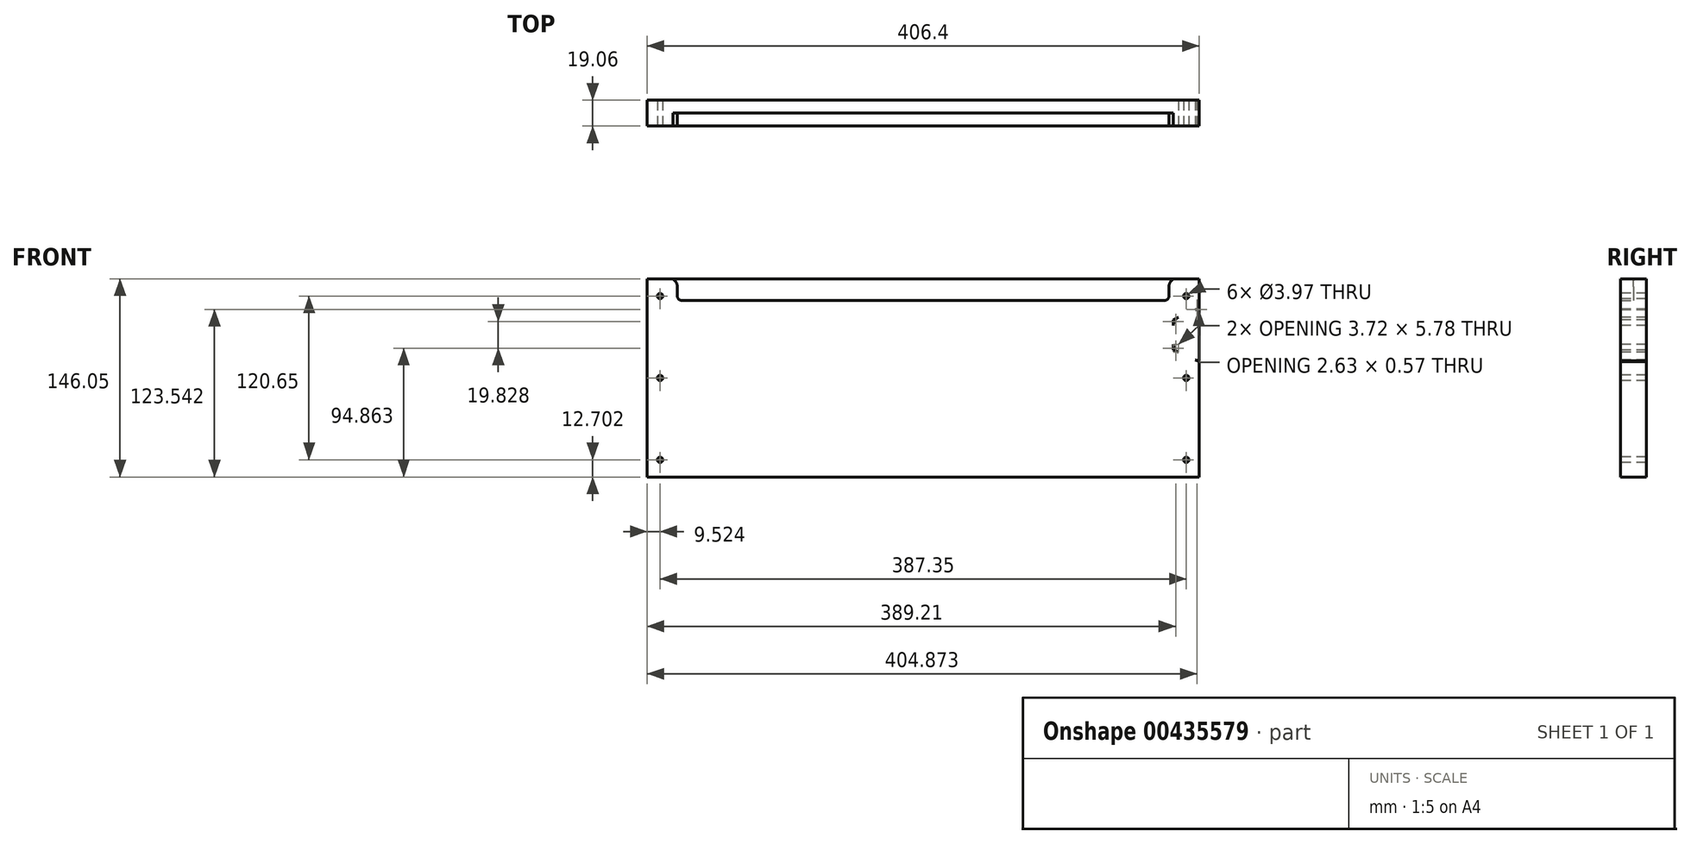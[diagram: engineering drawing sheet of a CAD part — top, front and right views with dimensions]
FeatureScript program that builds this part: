
annotation { "Feature Type Name" : "Feature", "Feature Type Description" : "" }
export const myFeature = defineFeature(function(context is Context, id is Id, definition is map)
    precondition{}
    {
        {
            var Q0;
            Q0=qCreatedBy(makeId("Front.planeOp"),FACE);
            var sketch = newSketch(context, id + "F0", { "sketchPlane" : qUnion([Q0])});
            skLineSegment(sketch, "E0", {"start": v(160.66, 42.77) * mm, "end": v(160.66, 55.47) * mm});
            skLineSegment(sketch, "E1.right", {"start": v(182.89, 55.47) * mm, "end": v(182.89, -90.58) * mm});
            skLineSegment(sketch, "E2", {"start": v(182.89, -30.25) * mm, "end": v(182.68, -30.25) * mm});
            skLineSegment(sketch, "E3", {"start": v(180.05, -30.82) * mm, "end": v(167.56, -36.5) * mm});
            skLineSegment(sketch, "E4", {"start": v(163.84, -42.28) * mm, "end": v(163.84, -56.33) * mm});
            skLineSegment(sketch, "E5", {"start": v(167.56, -62.1) * mm, "end": v(180.05, -67.78) * mm});
            skLineSegment(sketch, "E6", {"start": v(182.68, -68.35) * mm, "end": v(182.89, -68.35) * mm});
            skPoint(sketch, "E7.visualSharp", {"position": v(181.3, -30.25) * mm});
            skArc(sketch, "E7.filletArc", {"start": v(182.68, -30.25) * mm, "mid": v(181.33, -30.4) * mm, "end": v(180.05, -30.82) * mm});
            skPoint(sketch, "E8.visualSharp", {"position": v(163.84, -38.2) * mm});
            skArc(sketch, "E8.filletArc", {"start": v(167.56, -36.5) * mm, "mid": v(164.85, -38.84) * mm, "end": v(163.84, -42.28) * mm});
            skPoint(sketch, "E9.visualSharp", {"position": v(163.84, -60.42) * mm});
            skArc(sketch, "E9.filletArc", {"start": v(163.84, -56.33) * mm, "mid": v(164.85, -59.76) * mm, "end": v(167.56, -62.1) * mm});
            skPoint(sketch, "E10.visualSharp", {"position": v(181.3, -68.35) * mm});
            skArc(sketch, "E10.filletArc", {"start": v(180.05, -67.78) * mm, "mid": v(181.33, -68.2) * mm, "end": v(182.68, -68.35) * mm});
            skLineSegment(sketch, "E11.MirrorCS", {"start": v(-223.51, 55.47) * mm, "end": v(-223.51, -90.58) * mm});
            skArc(sketch, "E12.filletArc", {"start": v(-201.29, 42.77) * mm, "mid": v(-200.36, 40.53) * mm, "end": v(-198.11, 39.6) * mm});
            skArc(sketch, "E13.filletArc", {"start": v(157.49, 39.6) * mm, "mid": v(159.73, 40.53) * mm, "end": v(160.66, 42.77) * mm});
            skLineSegment(sketch, "E14.MirrorCS", {"start": v(182.68, 33.25) * mm, "end": v(182.89, 33.25) * mm});
            skLineSegment(sketch, "E15.MirrorCS", {"start": v(182.89, -4.85) * mm, "end": v(182.68, -4.85) * mm});
            skArc(sketch, "E16.MirrorCS", {"start": v(180.05, 32.68) * mm, "mid": v(181.33, 33.1) * mm, "end": v(182.68, 33.25) * mm});
            skArc(sketch, "E17.MirrorCS", {"start": v(182.68, -4.85) * mm, "mid": v(181.33, -4.7) * mm, "end": v(180.05, -4.28) * mm});
            skArc(sketch, "E18.MirrorCS", {"start": v(163.84, 21.22) * mm, "mid": v(164.85, 24.66) * mm, "end": v(167.56, 27) * mm});
            skLineSegment(sketch, "E19.MirrorCS", {"start": v(157.45, 22.4) * mm, "end": v(189.24, 36.85) * mm});
            skLineSegment(sketch, "E20.MirrorCS", {"start": v(189.24, -8.46) * mm, "end": v(157.45, 5.99) * mm});
            skLineSegment(sketch, "E21.MirrorCS", {"start": v(189.24, -4.85) * mm, "end": v(173.36, -4.85) * mm});
            skLineSegment(sketch, "E22.MirrorCS", {"start": v(173.36, 33.25) * mm, "end": v(189.24, 33.25) * mm});
            skArc(sketch, "E23.MirrorCS", {"start": v(167.56, 1.4) * mm, "mid": v(164.85, 3.74) * mm, "end": v(163.84, 7.17) * mm});
            skLineSegment(sketch, "E24.MirrorCS", {"start": v(180.05, -4.28) * mm, "end": v(167.56, 1.4) * mm});
            skLineSegment(sketch, "E25.MirrorCS", {"start": v(163.84, 7.17) * mm, "end": v(163.84, 21.22) * mm});
            skLineSegment(sketch, "E26.MirrorCS", {"start": v(167.56, 27) * mm, "end": v(180.05, 32.68) * mm});
            skLineSegment(sketch, "E27.MirrorCS", {"start": v(163.84, -1.68) * mm, "end": v(163.84, 36.42) * mm});
            skPoint(sketch, "E28.MirrorP", {"position": v(181.3, -4.85) * mm});
            skPoint(sketch, "E29.MirrorP", {"position": v(163.84, 25.3) * mm});
            skPoint(sketch, "E30.MirrorP", {"position": v(163.84, 3.08) * mm});
            skPoint(sketch, "E31.MirrorP", {"position": v(181.3, 33.25) * mm});
            skLineSegment(sketch, "E32.MirrorCS", {"start": v(-223.3, 33.25) * mm, "end": v(-223.51, 33.25) * mm});
            skLineSegment(sketch, "E33.MirrorCS", {"start": v(-223.51, -4.85) * mm, "end": v(-223.3, -4.85) * mm});
            skLineSegment(sketch, "E34.MirrorCS", {"start": v(-223.3, -68.35) * mm, "end": v(-223.51, -68.35) * mm});
            skArc(sketch, "E35.MirrorCS", {"start": v(-223.3, -30.25) * mm, "mid": v(-221.95, -30.4) * mm, "end": v(-220.67, -30.82) * mm});
            skArc(sketch, "E36.MirrorCS", {"start": v(-220.67, 32.68) * mm, "mid": v(-221.95, 33.1) * mm, "end": v(-223.3, 33.25) * mm});
            skArc(sketch, "E37.MirrorCS", {"start": v(-223.3, -4.85) * mm, "mid": v(-221.95, -4.7) * mm, "end": v(-220.67, -4.28) * mm});
            skArc(sketch, "E38.MirrorCS", {"start": v(-220.67, -67.78) * mm, "mid": v(-221.95, -68.2) * mm, "end": v(-223.3, -68.35) * mm});
            skLineSegment(sketch, "E39.MirrorCS", {"start": v(-223.51, -30.25) * mm, "end": v(-223.3, -30.25) * mm});
            skArc(sketch, "E40.MirrorCS", {"start": v(-208.18, -36.5) * mm, "mid": v(-205.47, -38.84) * mm, "end": v(-204.46, -42.28) * mm});
            skLineSegment(sketch, "E41.MirrorCS", {"start": v(-220.67, -4.28) * mm, "end": v(-208.18, 1.4) * mm});
            skArc(sketch, "E42.MirrorCS", {"start": v(-208.18, 1.4) * mm, "mid": v(-205.47, 3.74) * mm, "end": v(-204.46, 7.17) * mm});
            skArc(sketch, "E43.MirrorCS", {"start": v(-204.46, -56.33) * mm, "mid": v(-205.47, -59.76) * mm, "end": v(-208.18, -62.1) * mm});
            skArc(sketch, "E44.MirrorCS", {"start": v(-204.46, 21.22) * mm, "mid": v(-205.47, 24.66) * mm, "end": v(-208.18, 27) * mm});
            skLineSegment(sketch, "E45.MirrorCS", {"start": v(-220.67, -30.82) * mm, "end": v(-208.18, -36.5) * mm});
            skLineSegment(sketch, "E46.MirrorCS", {"start": v(-208.18, 27) * mm, "end": v(-220.67, 32.68) * mm});
            skLineSegment(sketch, "E47.MirrorCS", {"start": v(-208.18, -62.1) * mm, "end": v(-220.67, -67.78) * mm});
            skPoint(sketch, "E48.MirrorP", {"position": v(-204.46, 3.08) * mm});
            skPoint(sketch, "E49.MirrorP", {"position": v(-204.46, -38.2) * mm});
            skPoint(sketch, "E50.MirrorP", {"position": v(-221.92, 33.25) * mm});
            skPoint(sketch, "E51.MirrorP", {"position": v(-204.46, 25.3) * mm});
            skLineSegment(sketch, "E52.MirrorCS", {"start": v(-204.46, 7.17) * mm, "end": v(-204.46, 21.22) * mm});
            skPoint(sketch, "E53.MirrorP", {"position": v(-221.92, -68.35) * mm});
            skPoint(sketch, "E54.MirrorP", {"position": v(-204.46, -60.42) * mm});
            skLineSegment(sketch, "E55.MirrorCS", {"start": v(-204.46, -42.28) * mm, "end": v(-204.46, -56.33) * mm});
            skPoint(sketch, "E56.MirrorP", {"position": v(-221.92, -30.25) * mm});
            skPoint(sketch, "E57.MirrorP", {"position": v(-221.92, -4.85) * mm});
            skCircle(sketch, "E58", {"center": v(173.36, -77.88) * mm, "radius": 1.98 * mm});
            skCircle(sketch, "E59", {"center": v(173.36, -17.55) * mm, "radius": 1.98 * mm});
            skCircle(sketch, "E60.MirrorC", {"center": v(173.36, 42.77) * mm, "radius": 1.98 * mm});
            skCircle(sketch, "E61.MirrorC", {"center": v(-213.99, -77.88) * mm, "radius": 1.98 * mm});
            skCircle(sketch, "E62.MirrorC", {"center": v(-213.99, -17.55) * mm, "radius": 1.98 * mm});
            skCircle(sketch, "E63.MirrorC", {"center": v(-213.99, 42.77) * mm, "radius": 1.98 * mm});
            skLineSegment(sketch, "E64", {"start": v(-201.29, 55.47) * mm, "end": v(-201.29, 42.77) * mm});
            skLineSegment(sketch, "E65", {"start": v(-223.51, 55.47) * mm, "end": v(182.89, 55.47) * mm});
            skLineSegment(sketch, "E66", {"start": v(157.49, 39.6) * mm, "end": v(-198.11, 39.6) * mm});
            skLineSegment(sketch, "E67", {"start": v(-223.51, -90.58) * mm, "end": v(182.89, -90.58) * mm});
            skLineSegment(sketch, "E68", {"start": v(-223.51, -17.55) * mm, "end": v(182.89, -17.55) * mm, "construction": true});
            skLineSegment(sketch, "E69", {"start": v(-20.31, -90.58) * mm, "end": v(-20.31, 55.47) * mm, "construction": true});
            skSolve(sketch);
        }
        {
            var Q0;
            {var subQ22=sQuery(id+"F0.wireOp",EDGE,"E0");Q0=makeQuery(id+"F0.imprint","IMPRINT",FACE,{"disambiguationData":[TD([[makeQuery(id+"F0.imprint","IMPRINT",EDGE,{"derivedFrom":subQ22}),-1.0]])]});}
            var Q1;
            {var subQ1=sQuery(id+"F0.wireOp",EDGE,"E0");Q1=makeQuery(id+"F0.imprint","IMPRINT",FACE,{"disambiguationData":[TD([[makeQuery(id+"F0.imprint","IMPRINT",EDGE,{"derivedFrom":subQ1}),1.0]])]});}
            var Q2;
            {var subQ0=sQuery(id+"F0.wireOp",EDGE,"E21.MirrorCS");var subQ1=sQuery(id+"F0.wireOp",EDGE,"E1.right");var subQ2=makeQuery(id+"F0.imprint","INTERSECT",VERTEX,{"derivedFrom":[subQ1,subQ0]});Q2=makeQuery(id+"F0.imprint","IMPRINT",FACE,{"disambiguationData":[TD([[makeQuery(id+"F0.imprint","IMPRINT",EDGE,{"disambiguationData":[TD([[subQ2,-1.0]])],"derivedFrom":subQ1}),-1.0]])]});}
            var Q3;
            {var subQ0=sQuery(id+"F0.wireOp",EDGE,"E17.MirrorCS");Q3=makeQuery(id+"F0.imprint","IMPRINT",FACE,{"disambiguationData":[TD([[makeQuery(id+"F0.imprint","IMPRINT",EDGE,{"derivedFrom":subQ0}),1.0]])]});}
            var Q4;
            {var subQ0=sQuery(id+"F0.wireOp",EDGE,"E23.MirrorCS");Q4=makeQuery(id+"F0.imprint","IMPRINT",FACE,{"disambiguationData":[TD([[makeQuery(id+"F0.imprint","IMPRINT",EDGE,{"derivedFrom":subQ0}),1.0]])]});}
            var Q5;
            {var subQ0=sQuery(id+"F0.wireOp",EDGE,"E18.MirrorCS");Q5=makeQuery(id+"F0.imprint","IMPRINT",FACE,{"disambiguationData":[TD([[makeQuery(id+"F0.imprint","IMPRINT",EDGE,{"derivedFrom":subQ0}),1.0]])]});}
            var Q6;
            {var subQ0=sQuery(id+"F0.wireOp",EDGE,"E19.MirrorCS");var subQ1=sQuery(id+"F0.wireOp",EDGE,"E1.right");var subQ2=makeQuery(id+"F0.imprint","INTERSECT",VERTEX,{"derivedFrom":[subQ1,subQ0]});Q6=makeQuery(id+"F0.imprint","IMPRINT",FACE,{"disambiguationData":[TD([[makeQuery(id+"F0.imprint","IMPRINT",EDGE,{"disambiguationData":[TD([[subQ2,-1.0]])],"derivedFrom":subQ1}),-1.0]])]});}
            var Q7;
            {var subQ0=sQuery(id+"F0.wireOp",EDGE,"E16.MirrorCS");Q7=makeQuery(id+"F0.imprint","IMPRINT",FACE,{"disambiguationData":[TD([[makeQuery(id+"F0.imprint","IMPRINT",EDGE,{"derivedFrom":subQ0}),1.0]])]});}
            extrude(context, id + "F1", {"entities" : qUnion([Q0, Q1, Q2, Q3, Q4, Q5, Q6, Q7]), "oppositeDirection" : true, "depth" : 9.52 * mm, "offsetDistance" : 25.4 * mm});
        }
        {
            var Q0;
            {var subQ22=sQuery(id+"F0.wireOp",EDGE,"E0");Q0=makeQuery(id+"F0.imprint","IMPRINT",FACE,{"disambiguationData":[TD([[makeQuery(id+"F0.imprint","IMPRINT",EDGE,{"derivedFrom":subQ22}),-1.0]])]});}
            var Q1;
            {var subQ0=sQuery(id+"F0.wireOp",EDGE,"E16.MirrorCS");Q1=makeQuery(id+"F0.imprint","IMPRINT",FACE,{"disambiguationData":[TD([[makeQuery(id+"F0.imprint","IMPRINT",EDGE,{"derivedFrom":subQ0}),1.0]])]});}
            var Q2;
            {var subQ0=sQuery(id+"F0.wireOp",EDGE,"E19.MirrorCS");var subQ1=sQuery(id+"F0.wireOp",EDGE,"E1.right");var subQ2=makeQuery(id+"F0.imprint","INTERSECT",VERTEX,{"derivedFrom":[subQ1,subQ0]});Q2=makeQuery(id+"F0.imprint","IMPRINT",FACE,{"disambiguationData":[TD([[makeQuery(id+"F0.imprint","IMPRINT",EDGE,{"disambiguationData":[TD([[subQ2,-1.0]])],"derivedFrom":subQ1}),-1.0]])]});}
            var Q3;
            {var subQ0=sQuery(id+"F0.wireOp",EDGE,"E18.MirrorCS");Q3=makeQuery(id+"F0.imprint","IMPRINT",FACE,{"disambiguationData":[TD([[makeQuery(id+"F0.imprint","IMPRINT",EDGE,{"derivedFrom":subQ0}),1.0]])]});}
            var Q4;
            {var subQ0=sQuery(id+"F0.wireOp",EDGE,"E23.MirrorCS");Q4=makeQuery(id+"F0.imprint","IMPRINT",FACE,{"disambiguationData":[TD([[makeQuery(id+"F0.imprint","IMPRINT",EDGE,{"derivedFrom":subQ0}),1.0]])]});}
            var Q5;
            {var subQ0=sQuery(id+"F0.wireOp",EDGE,"E17.MirrorCS");Q5=makeQuery(id+"F0.imprint","IMPRINT",FACE,{"disambiguationData":[TD([[makeQuery(id+"F0.imprint","IMPRINT",EDGE,{"derivedFrom":subQ0}),1.0]])]});}
            var Q6;
            {var subQ0=sQuery(id+"F0.wireOp",EDGE,"E21.MirrorCS");var subQ1=sQuery(id+"F0.wireOp",EDGE,"E1.right");var subQ2=makeQuery(id+"F0.imprint","INTERSECT",VERTEX,{"derivedFrom":[subQ1,subQ0]});Q6=makeQuery(id+"F0.imprint","IMPRINT",FACE,{"disambiguationData":[TD([[makeQuery(id+"F0.imprint","IMPRINT",EDGE,{"disambiguationData":[TD([[subQ2,-1.0]])],"derivedFrom":subQ1}),-1.0]])]});}
            extrude(context, id + "F2", {"entities" : qUnion([Q0, Q1, Q2, Q3, Q4, Q5, Q6]), "operationType" : NewBodyOperationType.ADD, "depth" : 9.52 * mm, "offsetDistance" : 25.4 * mm});
        }
        {
            var Q0;
            Q0=makeQuery(id+"F2.opExtrude","SWEPT_EDGE",EDGE,{"disambiguationData":[OSD([sQuery(id+"F0.wireOp",EDGE,"E1.bottom"),sQuery(id+"F0.wireOp",EDGE,"E64")])]});
            var Q1;
            Q1=makeQuery(id+"F2.opExtrude","SWEPT_EDGE",EDGE,{"disambiguationData":[OSD([sQuery(id+"F0.wireOp",EDGE,"E0"),sQuery(id+"F0.wireOp",EDGE,"E1.bottom")])]});
            chamfer(context, id + "F3", {"entities" : qUnion([Q0, Q1]), "width" : 3.17 * mm, "tangentPropagation" : true});
        }
        {
            var Q0;
            {var subQ0=sQuery(id+"F0.wireOp",EDGE,"E0");Q0=makeQuery(id+"F3.opChamfer","BLEND_EDGE",EDGE,{"blendedFrom":[makeQuery(id+"F2.opExtrude","SWEPT_EDGE",EDGE,{"disambiguationData":[OSD([subQ0,sQuery(id+"F0.wireOp",EDGE,"E1.bottom")])]}),makeQuery(id+"F2.opExtrude","SWEPT_FACE",FACE,{"disambiguationData":[OSD([subQ0])]})],"blendedInto":[makeQuery(id+"F2.opExtrude","SWEPT_FACE",FACE,{"disambiguationData":[OSD([subQ0])]})]});}
            var Q1;
            {var subQ0=sQuery(id+"F0.wireOp",EDGE,"E64");Q1=makeQuery(id+"F3.opChamfer","BLEND_EDGE",EDGE,{"blendedFrom":[makeQuery(id+"F2.opExtrude","SWEPT_EDGE",EDGE,{"disambiguationData":[OSD([sQuery(id+"F0.wireOp",EDGE,"E1.bottom"),subQ0])]}),makeQuery(id+"F2.opExtrude","SWEPT_FACE",FACE,{"disambiguationData":[OSD([subQ0])]})],"blendedInto":[makeQuery(id+"F2.opExtrude","SWEPT_FACE",FACE,{"disambiguationData":[OSD([subQ0])]})]});}
            fillet(context, id + "F4", {"entities" : qUnion([Q0, Q1]), "radius" : 6.35 * mm, "tangentPropagation" : true, "allowEdgeOverflow" : false});
        }
    });
